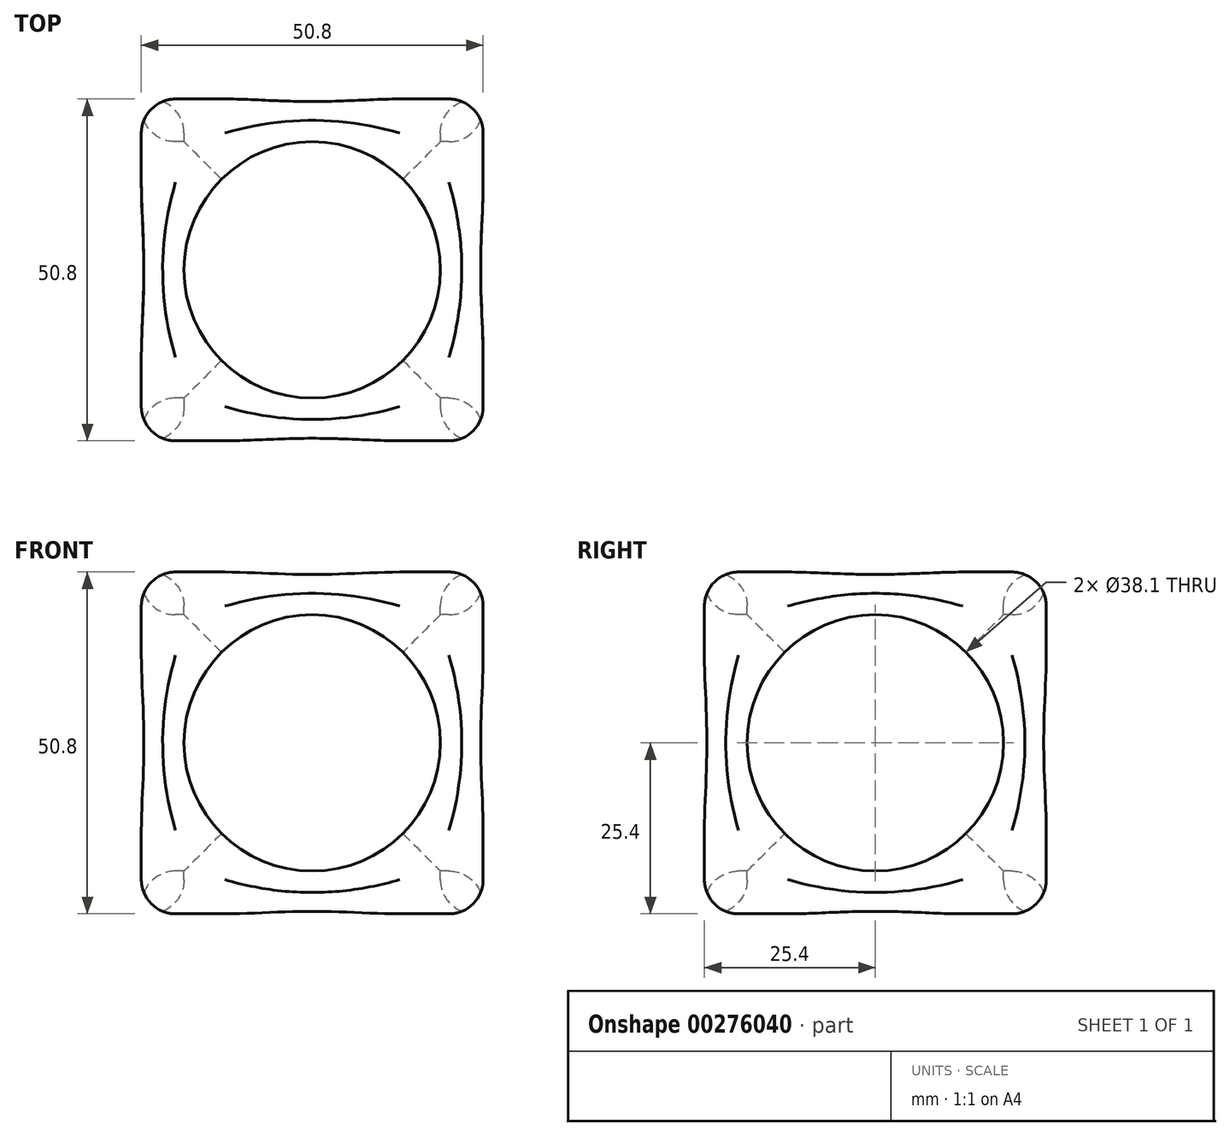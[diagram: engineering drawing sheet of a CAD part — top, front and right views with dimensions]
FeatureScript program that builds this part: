
annotation { "Feature Type Name" : "Feature", "Feature Type Description" : "" }
export const myFeature = defineFeature(function(context is Context, id is Id, definition is map)
    precondition{}
    {
        {
            var Q0;
            Q0=qCreatedBy(makeId("Front.planeOp"),FACE);
            var sketch = newSketch(context, id + "F0", { "sketchPlane" : qUnion([Q0])});
            skLineSegment(sketch, "E0.bottom", {"start": v(0, 0) * mm, "end": v(50.8, 0) * mm});
            skLineSegment(sketch, "E0.top", {"start": v(0, 50.8) * mm, "end": v(50.8, 50.8) * mm});
            skLineSegment(sketch, "E0.left", {"start": v(0, 0) * mm, "end": v(0, 50.8) * mm});
            skLineSegment(sketch, "E0.right", {"start": v(50.8, 0) * mm, "end": v(50.8, 50.8) * mm});
            skSolve(sketch);
        }
        {
            var Q0;
            Q0=qSketchRegion(id+"F0",true);
            extrude(context, id + "F1", {"entities" : qUnion([Q0]), "depth" : 50.8 * mm});
        }
        {
            var Q0;
            Q0=makeQuery(id+"F1.opExtrude","CAP_FACE",FACE,{"disambiguationData":[OSD([sQuery(id+"F0.wireOp",EDGE,"E0.bottom"),sQuery(id+"F0.wireOp",EDGE,"E0.top"),sQuery(id+"F0.wireOp",EDGE,"E0.left"),sQuery(id+"F0.wireOp",EDGE,"E0.right")])],"isStart":false});
            var sketch = newSketch(context, id + "F2", { "sketchPlane" : qUnion([Q0])});
            skCircle(sketch, "E1", {"center": v(25.4, 25.4) * mm, "radius": 19.05 * mm});
            skSolve(sketch);
        }
        {
            var Q0;
            Q0=qSketchRegion(id+"F2",true);
            extrude(context, id + "F3", {"entities" : qUnion([Q0]), "operationType" : NewBodyOperationType.REMOVE, "endBound" : BoundingType.THROUGH_ALL, "oppositeDirection" : true, "depth" : 25.4 * mm});
        }
        {
            var Q0;
            Q0=makeQuery(id+"F1.opExtrude","SWEPT_FACE",FACE,{"disambiguationData":[OSD([sQuery(id+"F0.wireOp",EDGE,"E0.top")])]});
            var sketch = newSketch(context, id + "F4", { "sketchPlane" : qUnion([Q0])});
            skCircle(sketch, "E2", {"center": v(25.4, -25.4) * mm, "radius": 19.05 * mm});
            skSolve(sketch);
        }
        {
            var Q0;
            Q0=qSketchRegion(id+"F4",true);
            extrude(context, id + "F5", {"entities" : qUnion([Q0]), "operationType" : NewBodyOperationType.REMOVE, "endBound" : BoundingType.THROUGH_ALL, "oppositeDirection" : true, "depth" : 25.4 * mm});
        }
        {
            var Q0;
            Q0=makeQuery(id+"F1.opExtrude","SWEPT_FACE",FACE,{"disambiguationData":[OSD([sQuery(id+"F0.wireOp",EDGE,"E0.left")])]});
            var sketch = newSketch(context, id + "F6", { "sketchPlane" : qUnion([Q0])});
            skCircle(sketch, "E3", {"center": v(25.4, 25.4) * mm, "radius": 19.05 * mm});
            skSolve(sketch);
        }
        {
            var Q0;
            Q0=qSketchRegion(id+"F6",true);
            extrude(context, id + "F7", {"entities" : qUnion([Q0]), "operationType" : NewBodyOperationType.REMOVE, "endBound" : BoundingType.THROUGH_ALL, "oppositeDirection" : true, "depth" : 25.4 * mm});
        }
        {
            var Q0;
            Q0=makeQuery(id+"F1.opExtrude","SWEPT_FACE",FACE,{"disambiguationData":[OSD([sQuery(id+"F0.wireOp",EDGE,"E0.left")])]});
            var Q1;
            Q1=makeQuery(id+"F1.opExtrude","CAP_FACE",FACE,{"disambiguationData":[OSD([sQuery(id+"F0.wireOp",EDGE,"E0.bottom"),sQuery(id+"F0.wireOp",EDGE,"E0.top"),sQuery(id+"F0.wireOp",EDGE,"E0.left"),sQuery(id+"F0.wireOp",EDGE,"E0.right")])],"isStart":true});
            var Q2;
            Q2=makeQuery(id+"F1.opExtrude","SWEPT_FACE",FACE,{"disambiguationData":[OSD([sQuery(id+"F0.wireOp",EDGE,"E0.right")])]});
            var Q3;
            Q3=makeQuery(id+"F1.opExtrude","CAP_FACE",FACE,{"disambiguationData":[OSD([sQuery(id+"F0.wireOp",EDGE,"E0.bottom"),sQuery(id+"F0.wireOp",EDGE,"E0.top"),sQuery(id+"F0.wireOp",EDGE,"E0.left"),sQuery(id+"F0.wireOp",EDGE,"E0.right")])],"isStart":false});
            var Q4;
            Q4=makeQuery(id+"F1.opExtrude","SWEPT_FACE",FACE,{"disambiguationData":[OSD([sQuery(id+"F0.wireOp",EDGE,"E0.bottom")])]});
            var Q5;
            Q5=makeQuery(id+"F1.opExtrude","SWEPT_FACE",FACE,{"disambiguationData":[OSD([sQuery(id+"F0.wireOp",EDGE,"E0.top")])]});
            fillet(context, id + "F8", {"entities" : qUnion([Q0, Q1, Q2, Q3, Q4, Q5]), "radius" : 5.08 * mm, "tangentPropagation" : true, "allowEdgeOverflow" : false});
        }
    });
